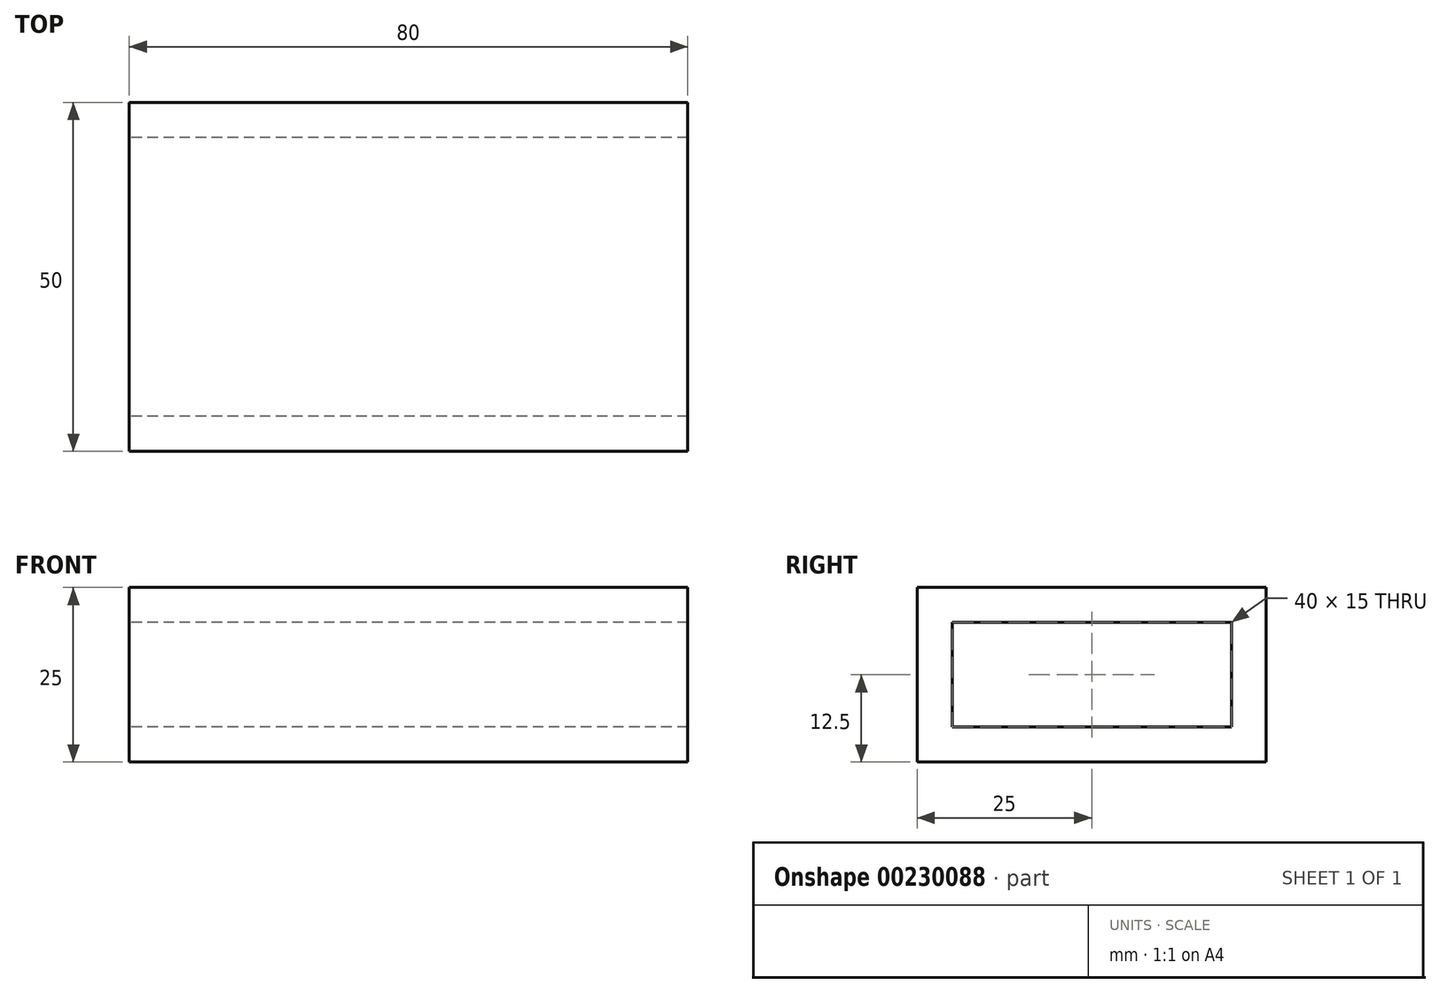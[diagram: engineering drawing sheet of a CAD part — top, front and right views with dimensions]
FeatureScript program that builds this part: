
annotation { "Feature Type Name" : "Feature", "Feature Type Description" : "" }
export const myFeature = defineFeature(function(context is Context, id is Id, definition is map)
    precondition{}
    {
        {
            var Q0;
            Q0=qCreatedBy(makeId("Right.planeOp"),FACE);
            var sketch = newSketch(context, id + "F0", { "sketchPlane" : qUnion([Q0])});
            skLineSegment(sketch, "E0.bottom", {"start": v(25, 12.5) * mm, "end": v(-25, 12.5) * mm});
            skLineSegment(sketch, "E0.top", {"start": v(25, -12.5) * mm, "end": v(-25, -12.5) * mm});
            skLineSegment(sketch, "E0.left", {"start": v(25, 12.5) * mm, "end": v(25, -12.5) * mm});
            skLineSegment(sketch, "E0.right", {"start": v(-25, 12.5) * mm, "end": v(-25, -12.5) * mm});
            skPoint(sketch, "E0.middle", {"position": v(0, 0) * mm});
            skLineSegment(sketch, "E1.bottom", {"start": v(20, 7.5) * mm, "end": v(-20, 7.5) * mm});
            skLineSegment(sketch, "E1.top", {"start": v(20, -7.5) * mm, "end": v(-20, -7.5) * mm});
            skLineSegment(sketch, "E1.left", {"start": v(20, 7.5) * mm, "end": v(20, -7.5) * mm});
            skLineSegment(sketch, "E1.right", {"start": v(-20, 7.5) * mm, "end": v(-20, -7.5) * mm});
            skSolve(sketch);
        }
        {
            var Q0;
            Q0=makeQuery(id+"F0.imprint","IMPRINT",FACE,{"disambiguationData":[TD([[makeQuery(id+"F0.imprint","IMPRINT",EDGE,{"derivedFrom":sQuery(id+"F0.wireOp",EDGE,"E0.bottom")}),1.0]])]});
            extrude(context, id + "F1", {"entities" : qUnion([Q0]), "endBound" : BoundingType.SYMMETRIC, "depth" : 80 * mm});
        }
    });
